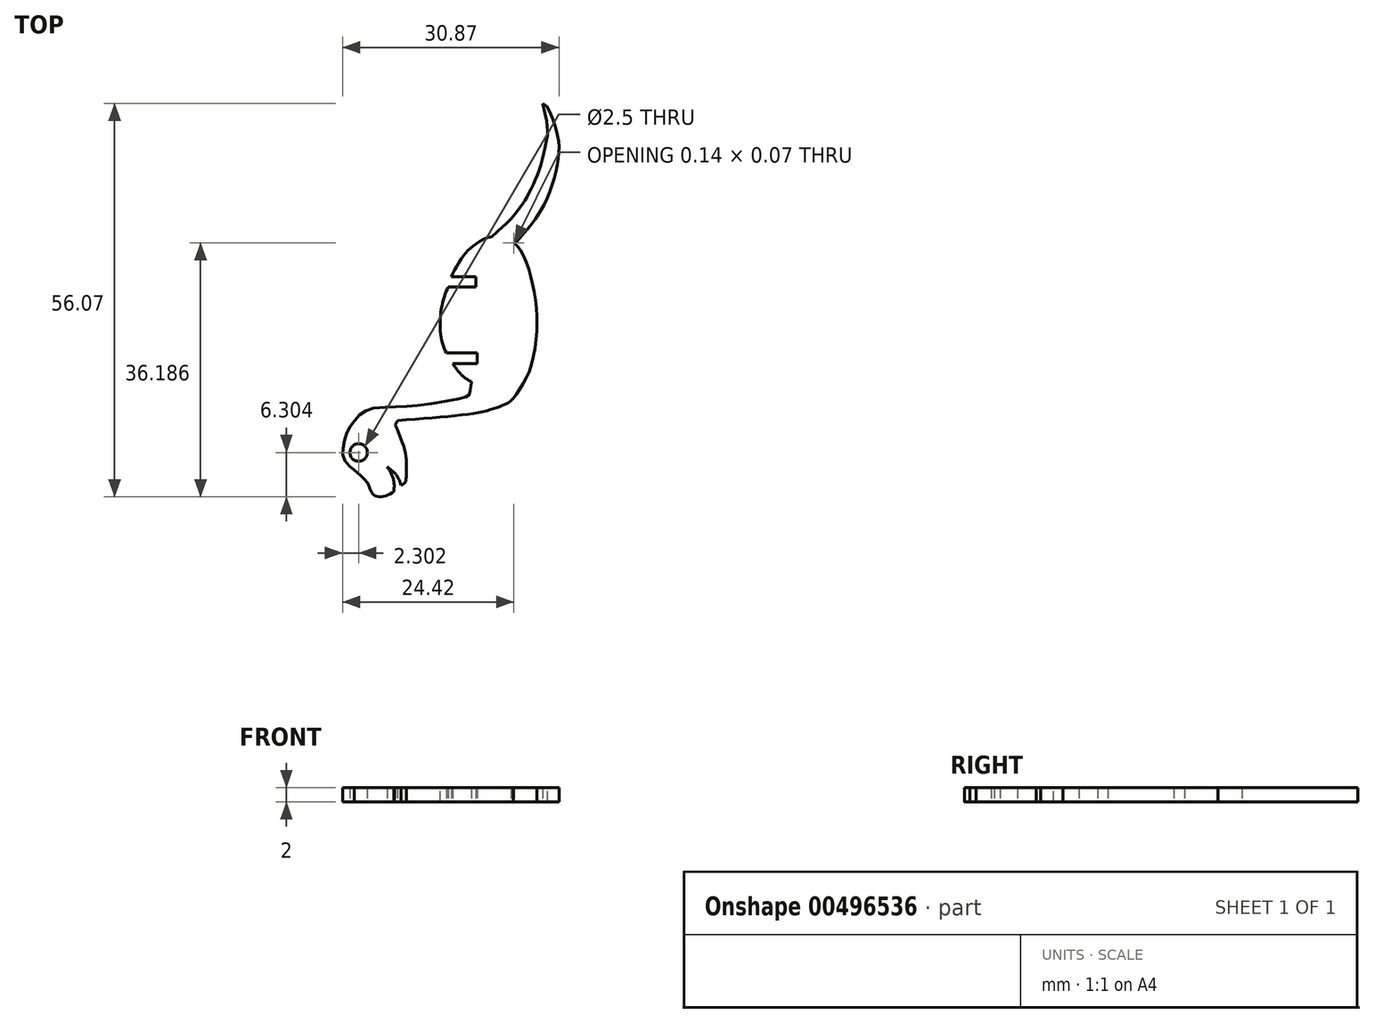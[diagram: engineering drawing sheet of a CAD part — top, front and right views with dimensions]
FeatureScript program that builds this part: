
annotation { "Feature Type Name" : "Feature", "Feature Type Description" : "" }
export const myFeature = defineFeature(function(context is Context, id is Id, definition is map)
    precondition{}
    {
        {
            var Q0;
            Q0=qCreatedBy(makeId("Top.planeOp"),FACE);
            var sketch = newSketch(context, id + "F0", { "sketchPlane" : qUnion([Q0])});
            skFitSpline(sketch, "E0", {"points": [v(17.41, 8) * mm, v(16.9, 9.26) * mm, v(15.45, 10.63) * mm], "startDerivative": vector(-0.77, 2.86) * mm, "endDerivative": vector(-3.09, 2.4) * mm});
            skFitSpline(sketch, "E1", {"points": [v(15.45, 10.63) * mm, v(16.32, 8.96) * mm, v(16.42, 7.1) * mm], "startDerivative": vector(2.13, -3.23) * mm, "endDerivative": vector(-0.19, -3.82) * mm});
            skFitSpline(sketch, "E2", {"points": [v(16.42, 7.1) * mm, v(15.54, 6.61) * mm, v(14.68, 6.38) * mm, v(13.82, 6.45) * mm, v(13.37, 6.82) * mm, v(13.08, 7.32) * mm, v(12.81, 7.98) * mm, v(12.5, 8.54) * mm, v(10.78, 10.15) * mm], "startDerivative": vector(-6.64, -4.08) * mm, "endDerivative": vector(-10.4, 8.86) * mm});
            skFitSpline(sketch, "E3", {"points": [v(10.78, 10.15) * mm, v(10.1, 10.71) * mm, v(9.38, 11.56) * mm, v(9.09, 12.42) * mm, v(9.16, 13.4) * mm, v(9.42, 14.66) * mm, v(9.95, 15.93) * mm, v(10.56, 16.87) * mm, v(11.38, 17.9) * mm, v(12.3, 18.52) * mm, v(13.6, 19.02) * mm, v(14.43, 19.08) * mm, v(15.1, 19.1) * mm, v(17.6, 19.22) * mm, v(20.15, 19.4) * mm, v(24.96, 20.18) * mm, v(26.51, 20.5) * mm, v(27, 20.73) * mm, v(27.19, 20.94) * mm, v(27.26, 21.27) * mm, v(27.48, 22.69) * mm], "startDerivative": vector(-15.89, 12.4) * mm, "endDerivative": vector(6, 61.42) * mm});
            skFitSpline(sketch, "E4", {"points": [v(27.48, 22.69) * mm, v(26.7, 23.2) * mm, v(25.97, 23.8) * mm, v(25.4, 24.48) * mm, v(24.8, 25.33) * mm], "startDerivative": vector(-2.13, 2.08) * mm, "endDerivative": vector(-2.24, 3.43) * mm});
            skFitSpline(sketch, "E5", {"points": [v(24.8, 25.33) * mm, v(28.3, 25.33) * mm], "startDerivative": vector(4.77, 0) * mm, "endDerivative": vector(4.77, 0) * mm});
            skFitSpline(sketch, "E6", {"points": [v(28.3, 25.33) * mm, v(28.3, 26.83) * mm], "startDerivative": vector(0, 1.55) * mm, "endDerivative": vector(0, 1.55) * mm});
            skFitSpline(sketch, "E7", {"points": [v(28.3, 26.83) * mm, v(23.9, 26.83) * mm], "startDerivative": vector(-5.68, 0) * mm, "endDerivative": vector(-5.68, 0) * mm});
            skFitSpline(sketch, "E8", {"points": [v(23.9, 26.83) * mm, v(23.47, 27.86) * mm, v(23.12, 29.2) * mm, v(23.01, 30.8) * mm, v(23.07, 32.29) * mm, v(23.3, 33.85) * mm, v(23.72, 35.25) * mm, v(24.18, 36.24) * mm], "startDerivative": vector(-3.32, 7.6) * mm, "endDerivative": vector(2.78, 5.9) * mm});
            skFitSpline(sketch, "E9", {"points": [v(24.18, 36.24) * mm, v(28.1, 36.24) * mm], "startDerivative": vector(6.4, 0) * mm, "endDerivative": vector(6.4, 0) * mm});
            skFitSpline(sketch, "E10", {"points": [v(28.1, 36.24) * mm, v(28.1, 37.74) * mm], "startDerivative": vector(0, 1.2) * mm, "endDerivative": vector(0, 1.2) * mm});
            skFitSpline(sketch, "E11", {"points": [v(28.1, 37.74) * mm, v(24.6, 37.74) * mm], "startDerivative": vector(-4.5, 0) * mm, "endDerivative": vector(-4.5, 0) * mm});
            skFitSpline(sketch, "E12", {"points": [v(24.6, 37.74) * mm, v(25.65, 39.67) * mm, v(26.78, 41.28) * mm, v(28.05, 42.37) * mm, v(29.52, 43.2) * mm, v(30.27, 43.4) * mm, v(30.67, 43.68) * mm, v(33.09, 45.95) * mm], "startDerivative": vector(2.72, 7.8) * mm, "endDerivative": vector(14.93, 14.1) * mm});
            skFitSpline(sketch, "E13", {"points": [v(33.09, 45.95) * mm, v(35.6, 49.5) * mm, v(37.1, 52.85) * mm, v(38.17, 57.13) * mm, v(37.64, 62.43) * mm], "startDerivative": vector(16.8, 19.48) * mm, "endDerivative": vector(-8.69, 36.62) * mm});
            skFitSpline(sketch, "E14", {"points": [v(17.41, 8) * mm, v(18.01, 8.39) * mm, v(18.16, 9.3) * mm, v(18.1, 12.26) * mm, v(16.63, 16.57) * mm], "startDerivative": vector(4.79, 2.1) * mm, "endDerivative": vector(-4.98, 11.56) * mm});
            skFitSpline(sketch, "E15", {"points": [v(16.63, 16.57) * mm, v(16.89, 17.22) * mm], "startDerivative": vector(0.26, 0.65) * mm, "endDerivative": vector(0.26, 0.65) * mm});
            skFitSpline(sketch, "E16", {"points": [v(16.89, 17.22) * mm, v(27.96, 18.27) * mm, v(30.92, 19) * mm, v(32.27, 19.51) * mm, v(33.46, 20.37) * mm], "startDerivative": vector(29.75, 2.3) * mm, "endDerivative": vector(10.76, 10.02) * mm});
            skFitSpline(sketch, "E17", {"points": [v(33.46, 20.37) * mm, v(34.09, 21.27) * mm, v(34.98, 22.74) * mm, v(35.8, 24.5) * mm, v(36.43, 27.07) * mm, v(36.77, 29.88) * mm, v(36.77, 32.18) * mm, v(36.52, 34.85) * mm, v(36, 37.4) * mm, v(35.37, 39.57) * mm, v(34.55, 41.32) * mm, v(33.92, 42.2) * mm, v(33.43, 42.58) * mm], "startDerivative": vector(11.82, 13.8) * mm, "endDerivative": vector(-12.88, 4.96) * mm});
            skFitSpline(sketch, "E18", {"points": [v(33.43, 42.58) * mm, v(33.64, 42.5) * mm, v(36.54, 45.93) * mm, v(38.97, 50.72) * mm, v(39.9, 54.98) * mm, v(39.63, 58.32) * mm, v(37.64, 62.43) * mm], "startDerivative": vector(10.4, -3.32) * mm, "endDerivative": vector(-12.88, 3.14) * mm});
            skCircle(sketch, "E19", {"center": v(11.38, 12.66) * mm, "radius": 1.25 * mm});
            skSolve(sketch);
        }
        {
            var Q0;
            Q0 = qSketchRegion(id + "F0", true);
            extrude(context, id + "F1", {"entities" : qUnion([Q0]), "depth" : 2 * mm, "offsetDistance" : 25 * mm});
        }
    });
